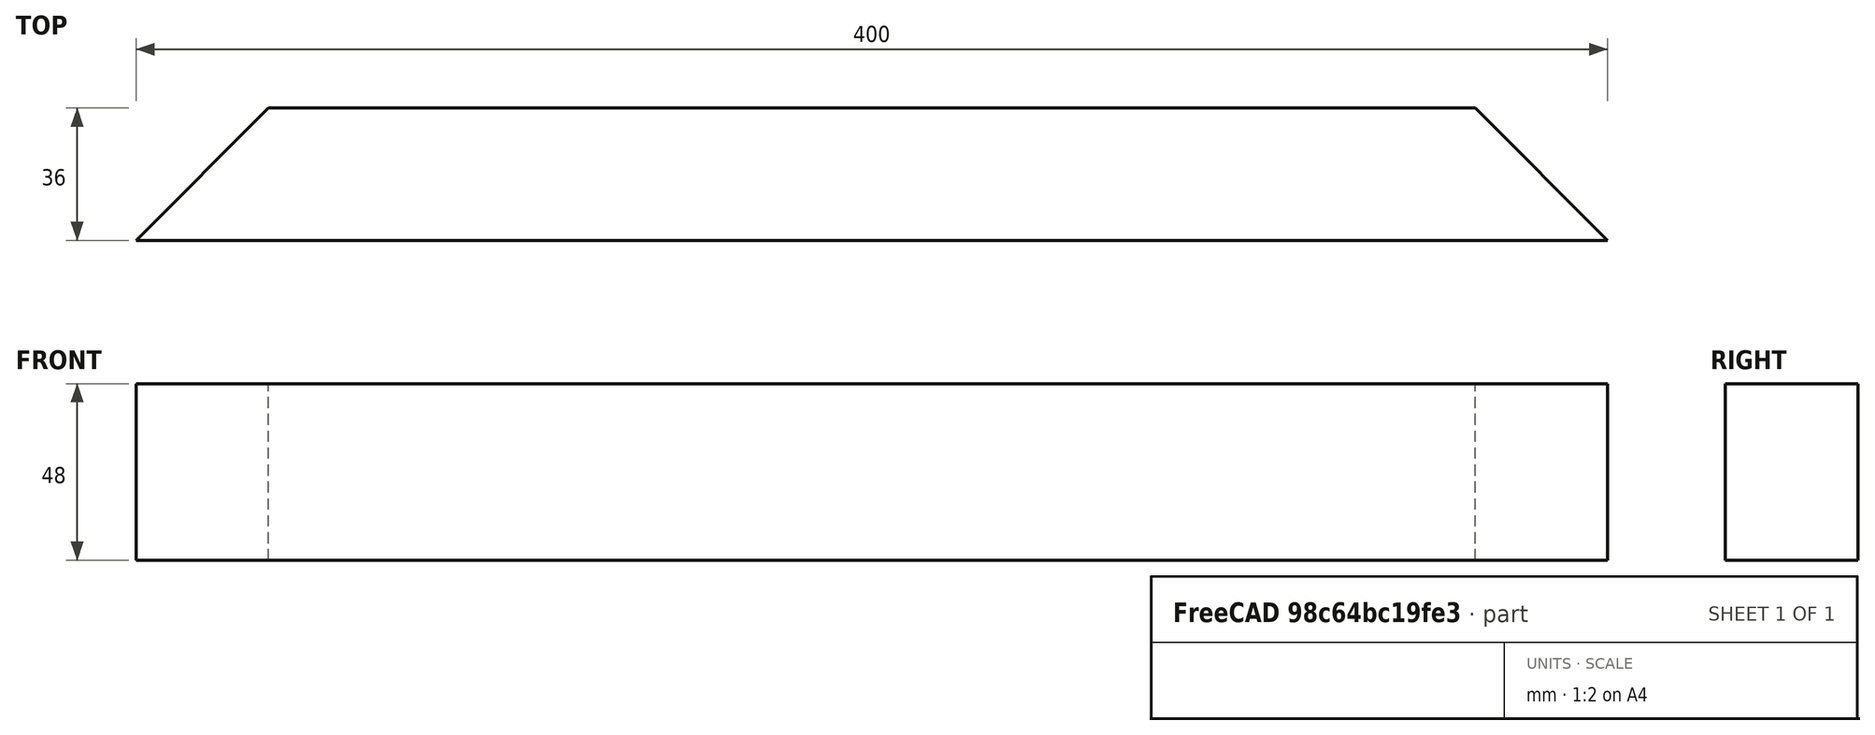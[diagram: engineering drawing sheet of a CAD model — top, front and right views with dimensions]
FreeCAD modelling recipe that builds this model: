
FCSTD DOCUMENT  (FreeCAD 0.19R24267 (Git))
Label: roofBase
License: Creative Commons Attribution-ShareAlike
LicenseURL: http://creativecommons.org/licenses/by-sa/4.0/
objects: Sketcher::SketchObject×1, Part::Extrusion×1
note: 2 computed .brp shape members not serialized (recipe doc carries the construction recipe); baked Part::Feature solids carry a one-line shape summary decoded from their .brp
EXTERNAL_REF file=Main.FCStd obj=Spreadsheet

FEATURE [Sketcher::SketchObject] Sketch
  FullyConstrained = true
  expr: Constraints[9] = Main#<<params>>.outerDeep
  expr: Constraints[8] = Main#<<params>>.structuralWoodHeight
  sketch-geometry (4):
    g0: LineSegment StartX=0 StartY=0 StartZ=0 EndX=36 EndY=36 EndZ=0
    g1: LineSegment StartX=36 StartY=36 StartZ=0 EndX=364 EndY=36 EndZ=0
    g2: LineSegment StartX=364 StartY=36 StartZ=0 EndX=400 EndY=0 EndZ=0
    g3: LineSegment StartX=400 StartY=0 StartZ=0 EndX=0 EndY=0 EndZ=0
  constraints (11):
    c: Coincident(g-1,g0)
    c: Coincident(g0,g1)
    c: Horizontal(g1)
    c: Coincident(g1,g2)
    c: PointOnObject(g2,g-1)
    c: Coincident(g2,g3)
    c: Coincident(g3,g0)
    c: Angle(g3,g0) = 0.785398
    c: DistanceY(g0,g0) = 36
    c: Distance(g3) = 400
    c: Equal(g0,g2)
FEATURE [Part::Extrusion] Extrude
  Base = -> Sketch
  Dir = (0,0,1)
  DirMode = 2
  FaceMakerClass = Part::FaceMakerBullseye
  LengthFwd = 48
  LengthRev = 0
  Solid = true
  Symmetric = false
  expr: LengthFwd = Main#<<params>>.structuralWoodWidth
